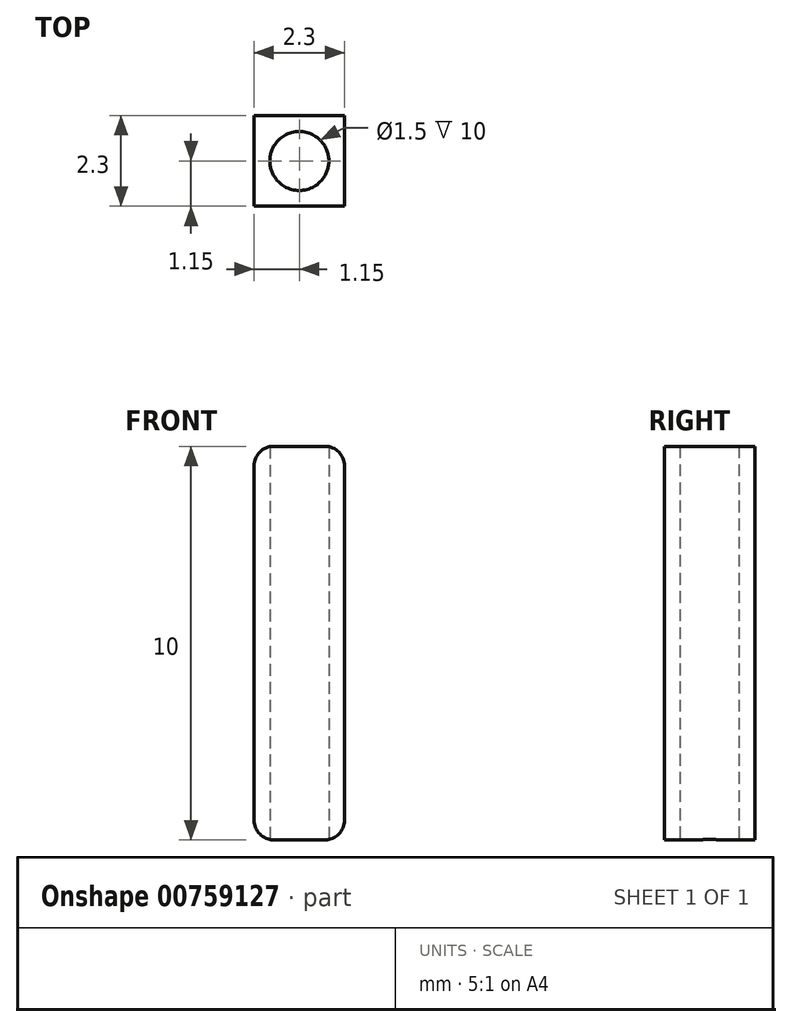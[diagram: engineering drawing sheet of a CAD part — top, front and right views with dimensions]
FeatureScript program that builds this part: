
annotation { "Feature Type Name" : "Feature", "Feature Type Description" : "" }
export const myFeature = defineFeature(function(context is Context, id is Id, definition is map)
    precondition{}
    {
        {
            var Q0;
            Q0=qCreatedBy(makeId("Top.planeOp"),FACE);
            var sketch = newSketch(context, id + "F0", { "sketchPlane" : qUnion([Q0])});
            skLineSegment(sketch, "E0.bottom", {"start": v(1.15, -1.15) * mm, "end": v(-1.15, -1.15) * mm});
            skLineSegment(sketch, "E0.top", {"start": v(1.15, 1.15) * mm, "end": v(-1.15, 1.15) * mm});
            skLineSegment(sketch, "E0.left", {"start": v(1.15, -1.15) * mm, "end": v(1.15, 1.15) * mm});
            skLineSegment(sketch, "E0.right", {"start": v(-1.15, -1.15) * mm, "end": v(-1.15, 1.15) * mm});
            skPoint(sketch, "E0.middle", {"position": v(0, 0) * mm});
            skCircle(sketch, "E1", {"center": v(0, 0) * mm, "radius": 0.75 * mm});
            skSolve(sketch);
        }
        {
            var Q0;
            Q0 = qSketchRegion(id + "F0", true);
            extrude(context, id + "F1", {"entities" : qUnion([Q0]), "depth" : 10 * mm, "offsetDistance" : 25 * mm});
        }
        {
            var Q0;
            Q0=makeQuery(id+"F1.opExtrude","CAP_EDGE",EDGE,{"disambiguationData":[OSD([sQuery(id+"F0.wireOp",EDGE,"E0.left")])],"isStart":false});
            var Q1;
            Q1=makeQuery(id+"F1.opExtrude","CAP_EDGE",EDGE,{"disambiguationData":[OSD([sQuery(id+"F0.wireOp",EDGE,"E0.right")])],"isStart":false});
            var Q2;
            Q2=makeQuery(id+"F1.opExtrude","CAP_EDGE",EDGE,{"disambiguationData":[OSD([sQuery(id+"F0.wireOp",EDGE,"E0.left")])],"isStart":true});
            var Q3;
            Q3=makeQuery(id+"F1.opExtrude","CAP_EDGE",EDGE,{"disambiguationData":[OSD([sQuery(id+"F0.wireOp",EDGE,"E0.right")])],"isStart":true});
            fillet(context, id + "F2", {"entities" : qUnion([Q0, Q1, Q2, Q3]), "radius" : 0.5 * mm, "tangentPropagation" : true, "allowEdgeOverflow" : false});
        }
    });
